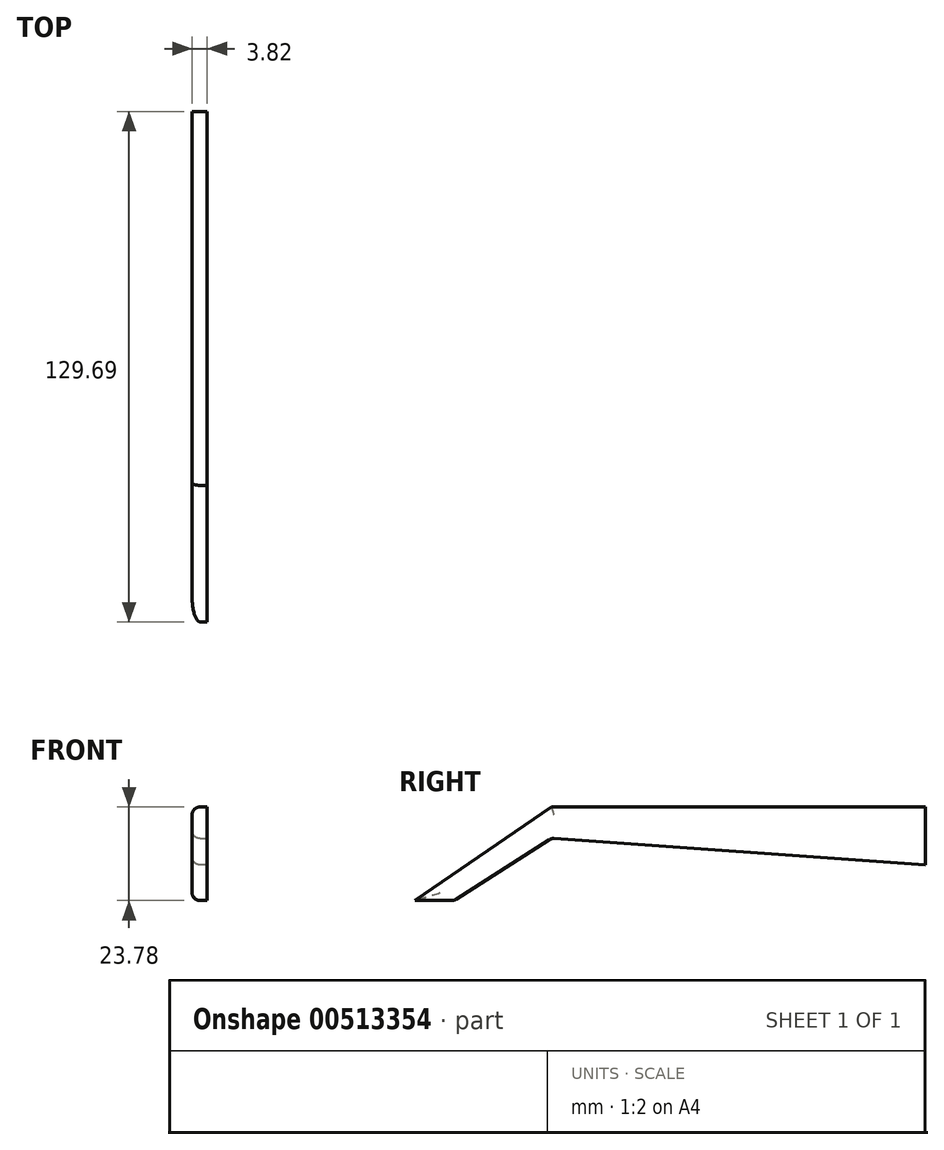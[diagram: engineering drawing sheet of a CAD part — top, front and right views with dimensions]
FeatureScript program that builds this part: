
annotation { "Feature Type Name" : "Feature", "Feature Type Description" : "" }
export const myFeature = defineFeature(function(context is Context, id is Id, definition is map)
    precondition{}
    {
        {
            var Q0;
            Q0=qCreatedBy(makeId("Right.planeOp"),FACE);
            var sketch = newSketch(context, id + "F0", { "sketchPlane" : qUnion([Q0])});
            skLineSegment(sketch, "E0", {"start": v(33.3, 8) * mm, "end": v(33.3, -6.72) * mm});
            skLineSegment(sketch, "E1", {"start": v(-96.39, -15.78) * mm, "end": v(-86.39, -15.78) * mm});
            skLineSegment(sketch, "E2", {"start": v(33.3, 8) * mm, "end": v(-61.7, 8) * mm});
            skLineSegment(sketch, "E3", {"start": v(-61.7, 8) * mm, "end": v(-96.39, -15.78) * mm});
            skLineSegment(sketch, "E4", {"start": v(-86.39, -15.78) * mm, "end": v(-61.7, 0) * mm});
            skLineSegment(sketch, "E5", {"start": v(-61.7, 0) * mm, "end": v(33.3, -6.72) * mm});
            skSolve(sketch);
        }
        {
            var Q0;
            Q0=makeQuery(id+"F0.imprint","IMPRINT",FACE,{"disambiguationData":[TD([[makeQuery(id+"F0.imprint","IMPRINT",EDGE,{"derivedFrom":sQuery(id+"F0.wireOp",EDGE,"E0")}),-1.0]])]});
            extrude(context, id + "F1", {"entities" : qUnion([Q0]), "depth" : 3.82 * mm});
        }
        {
            var Q0;
            Q0=makeQuery(id+"F1.opExtrude","CAP_EDGE",EDGE,{"disambiguationData":[OSD([sQuery(id+"F0.wireOp",EDGE,"E2")])],"isStart":true});
            var Q1;
            Q1=makeQuery(id+"F1.opExtrude","CAP_EDGE",EDGE,{"disambiguationData":[OSD([sQuery(id+"F0.wireOp",EDGE,"E5")])],"isStart":true});
            var Q2;
            Q2=makeQuery(id+"F1.opExtrude","CAP_EDGE",EDGE,{"disambiguationData":[OSD([sQuery(id+"F0.wireOp",EDGE,"E3")])],"isStart":true});
            var Q3;
            Q3=makeQuery(id+"F1.opExtrude","CAP_EDGE",EDGE,{"disambiguationData":[OSD([sQuery(id+"F0.wireOp",EDGE,"E4")])],"isStart":true});
            var Q4;
            Q4=makeQuery(id+"F1.opExtrude","CAP_EDGE",EDGE,{"disambiguationData":[OSD([sQuery(id+"F0.wireOp",EDGE,"E1")])],"isStart":true});
            var Q5;
            Q5=makeQuery(id+"F1.opExtrude","SWEPT_EDGE",EDGE,{"disambiguationData":[OSD([sQuery(id+"F0.wireOp",EDGE,"E4"),sQuery(id+"F0.wireOp",EDGE,"E5")])]});
            var Q6;
            Q6=makeQuery(id+"F1.opExtrude","SWEPT_EDGE",EDGE,{"disambiguationData":[OSD([sQuery(id+"F0.wireOp",EDGE,"E1"),sQuery(id+"F0.wireOp",EDGE,"E4")])]});
            fillet(context, id + "F2", {"entities" : qUnion([Q0, Q1, Q2, Q3, Q4, Q5, Q6]), "radius" : 2 * mm, "tangentPropagation" : true, "allowEdgeOverflow" : false});
        }
    });
